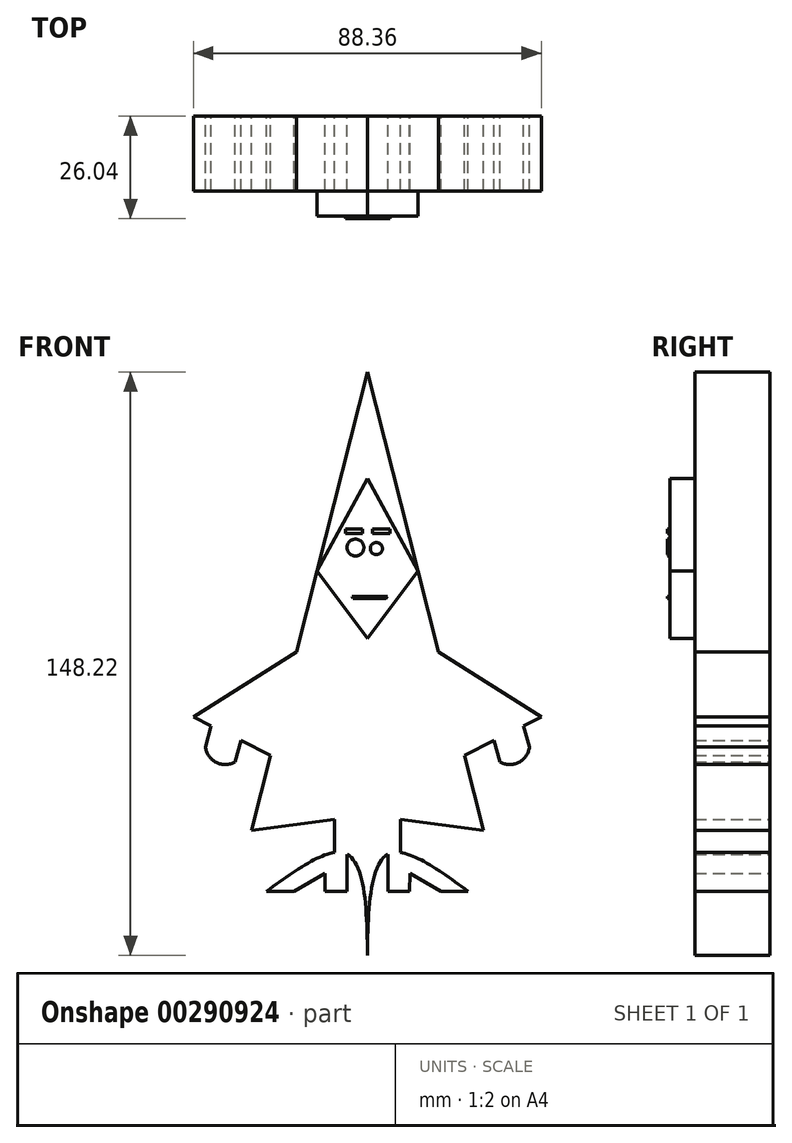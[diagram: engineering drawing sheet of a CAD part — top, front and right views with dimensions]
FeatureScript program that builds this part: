
annotation { "Feature Type Name" : "Feature", "Feature Type Description" : "" }
export const myFeature = defineFeature(function(context is Context, id is Id, definition is map)
    precondition{}
    {
        {
            var Q0;
            Q0=qCreatedBy(makeId("Front.planeOp"),FACE);
            var sketch = newSketch(context, id + "F0", { "sketchPlane" : qUnion([Q0])});
            skLineSegment(sketch, "E0", {"start": v(0, 75.5) * mm, "end": v(-12.78, 24.98) * mm});
            skLineSegment(sketch, "E1", {"start": v(-12.78, 24.98) * mm, "end": v(-17.99, 4.4) * mm});
            skLineSegment(sketch, "E2.MirrorCS", {"start": v(0, 75.5) * mm, "end": v(12.78, 24.98) * mm});
            skLineSegment(sketch, "E3.MirrorCS", {"start": v(12.78, 24.98) * mm, "end": v(17.99, 4.4) * mm});
            skLineSegment(sketch, "E4", {"start": v(-29.46, -40.92) * mm, "end": v(-8.36, -38.13) * mm});
            skLineSegment(sketch, "E5", {"start": v(-5.19, -37.7) * mm, "end": v(-5.19, -56.4) * mm});
            skLineSegment(sketch, "E6", {"start": v(-5.19, -56.4) * mm, "end": v(-10.75, -56.4) * mm});
            skLineSegment(sketch, "E7", {"start": v(-10.75, -56.4) * mm, "end": v(-10.75, -51.88) * mm});
            skLineSegment(sketch, "E8", {"start": v(-10.75, -51.88) * mm, "end": v(-18.7, -56.4) * mm});
            skLineSegment(sketch, "E9", {"start": v(-18.7, -56.4) * mm, "end": v(-25.6, -56.4) * mm});
            skFitSpline(sketch, "E10", {"points": [v(-25.6, -56.4) * mm, v(-5.19, -47.05) * mm, v(0, -78.15) * mm], "startDerivative": vector(52.64, 38.2) * mm, "endDerivative": vector(0.06, -78.44) * mm});
            skLineSegment(sketch, "E11", {"start": v(-8.36, -46.59) * mm, "end": v(-8.36, -38.13) * mm});
            skLineSegment(sketch, "E12", {"start": v(-17.99, 4.4) * mm, "end": v(-44.18, -12.07) * mm});
            skLineSegment(sketch, "E13", {"start": v(-44.18, -12.07) * mm, "end": v(-39.68, -14.35) * mm});
            skLineSegment(sketch, "E14", {"start": v(17.99, 4.4) * mm, "end": v(44.18, -12.07) * mm});
            skLineSegment(sketch, "E15", {"start": v(24.65, -21.93) * mm, "end": v(32.15, -18.15) * mm});
            skLineSegment(sketch, "E16.MirrorCS", {"start": v(5.19, -37.71) * mm, "end": v(5.17, -56.4) * mm});
            skLineSegment(sketch, "E17.MirrorCS", {"start": v(5.17, -56.4) * mm, "end": v(10.73, -56.4) * mm});
            skLineSegment(sketch, "E18.MirrorCS", {"start": v(8.35, -46.6) * mm, "end": v(8.36, -38.13) * mm});
            skFitSpline(sketch, "E19.MirrorCS", {"points": [v(25.6, -56.41) * mm, v(5.18, -47.05) * mm, v(-0.04, -78.15) * mm], "startDerivative": vector(-52.6, 38.25) * mm, "endDerivative": vector(-0.13, -78.44) * mm});
            skLineSegment(sketch, "E20.MirrorCS", {"start": v(10.73, -51.89) * mm, "end": v(18.7, -56.4) * mm});
            skLineSegment(sketch, "E21.MirrorCS", {"start": v(18.7, -56.4) * mm, "end": v(25.6, -56.41) * mm});
            skLineSegment(sketch, "E22.MirrorCS", {"start": v(10.73, -56.4) * mm, "end": v(10.73, -51.89) * mm});
            skLineSegment(sketch, "E23.trimOffspring", {"start": v(-24.65, -21.93) * mm, "end": v(-29.46, -40.92) * mm});
            skLineSegment(sketch, "E24.trimOffspring", {"start": v(24.65, -21.93) * mm, "end": v(29.46, -40.92) * mm});
            skLineSegment(sketch, "E25.trimOffspring", {"start": v(-5.19, -37.7) * mm, "end": v(0, -37.02) * mm});
            skLineSegment(sketch, "E26", {"start": v(0, -37.02) * mm, "end": v(5.19, -37.71) * mm});
            skLineSegment(sketch, "E27", {"start": v(8.36, -38.13) * mm, "end": v(29.46, -40.92) * mm});
            skLineSegment(sketch, "E28.trimOffspring", {"start": v(-32.15, -18.15) * mm, "end": v(-24.65, -21.93) * mm});
            skLineSegment(sketch, "E29.trimOffspring", {"start": v(39.68, -14.35) * mm, "end": v(44.18, -12.07) * mm});
            skLineSegment(sketch, "E30", {"start": v(-17.99, 4.4) * mm, "end": v(17.99, 4.4) * mm});
            skLineSegment(sketch, "E31", {"start": v(-39.68, -14.35) * mm, "end": v(-41.14, -19.7) * mm});
            skLineSegment(sketch, "E32", {"start": v(-32.15, -18.15) * mm, "end": v(-33.61, -23.5) * mm});
            skArc(sketch, "E33", {"start": v(-41.14, -19.7) * mm, "mid": v(-38.41, -23.67) * mm, "end": v(-33.61, -23.5) * mm});
            skLineSegment(sketch, "E34.MirrorCS", {"start": v(32.15, -18.15) * mm, "end": v(33.61, -23.5) * mm});
            skArc(sketch, "E35.MirrorCS", {"start": v(41.14, -19.7) * mm, "mid": v(38.41, -23.67) * mm, "end": v(33.61, -23.5) * mm});
            skLineSegment(sketch, "E36.MirrorCS", {"start": v(39.68, -14.35) * mm, "end": v(41.14, -19.7) * mm});
            skPoint(sketch, "E37.start.orphan", {"position": v(0, -5.3) * mm});
            skSolve(sketch);
        }
        {
            var Q0;
            Q0 = qSketchRegion(id + "F0", true);
            extrude(context, id + "F1", {"entities" : qUnion([Q0]), "depth" : 19.05 * mm});
        }
        {
            var Q0;
            Q0=makeQuery(id+"F1.opExtrude","CAP_FACE",FACE,{"disambiguationData":[OSD([sQuery(id+"F0.wireOp",EDGE,"E0"),sQuery(id+"F0.wireOp",EDGE,"E1"),sQuery(id+"F0.wireOp",EDGE,"E2.MirrorCS"),sQuery(id+"F0.wireOp",EDGE,"E3.MirrorCS"),sQuery(id+"F0.wireOp",EDGE,"E4"),sQuery(id+"F0.wireOp",EDGE,"E5"),sQuery(id+"F0.wireOp",EDGE,"E6"),sQuery(id+"F0.wireOp",EDGE,"E7"),sQuery(id+"F0.wireOp",EDGE,"E8"),sQuery(id+"F0.wireOp",EDGE,"E9"),sQuery(id+"F0.wireOp",EDGE,"E10"),sQuery(id+"F0.wireOp",EDGE,"E11"),sQuery(id+"F0.wireOp",EDGE,"E12"),sQuery(id+"F0.wireOp",EDGE,"E13"),sQuery(id+"F0.wireOp",EDGE,"E14"),sQuery(id+"F0.wireOp",EDGE,"E15"),sQuery(id+"F0.wireOp",EDGE,"E16.MirrorCS"),sQuery(id+"F0.wireOp",EDGE,"E17.MirrorCS"),sQuery(id+"F0.wireOp",EDGE,"E18.MirrorCS"),sQuery(id+"F0.wireOp",EDGE,"E19.MirrorCS"),sQuery(id+"F0.wireOp",EDGE,"E20.MirrorCS"),sQuery(id+"F0.wireOp",EDGE,"E21.MirrorCS"),sQuery(id+"F0.wireOp",EDGE,"E22.MirrorCS"),sQuery(id+"F0.wireOp",EDGE,"E23.trimOffspring"),sQuery(id+"F0.wireOp",EDGE,"E24.trimOffspring"),sQuery(id+"F0.wireOp",EDGE,"E25.trimOffspring"),sQuery(id+"F0.wireOp",EDGE,"E26"),sQuery(id+"F0.wireOp",EDGE,"E27")])],"isStart":false});
            var sketch = newSketch(context, id + "F2", { "sketchPlane" : qUnion([Q0])});
            skLineSegment(sketch, "E38", {"start": v(0, 48.43) * mm, "end": v(-12.78, 25) * mm});
            skLineSegment(sketch, "E39", {"start": v(-12.78, 25) * mm, "end": v(0, 7.83) * mm});
            skLineSegment(sketch, "E40", {"start": v(0, 7.83) * mm, "end": v(12.78, 25) * mm});
            skLineSegment(sketch, "E41", {"start": v(12.78, 25) * mm, "end": v(0, 48.43) * mm});
            skLineSegment(sketch, "E42", {"start": v(-17.99, 4.4) * mm, "end": v(-29.46, -40.92) * mm});
            skLineSegment(sketch, "E43", {"start": v(17.99, 4.4) * mm, "end": v(24.65, -21.93) * mm});
            skSolve(sketch);
        }
        {
            var Q0;
            Q0 = qSketchRegion(id + "F2", true);
            extrude(context, id + "F3", {"entities" : qUnion([Q0]), "operationType" : NewBodyOperationType.ADD, "depth" : 6.35 * mm});
        }
        {
            var Q0;
            Q0=makeQuery(id+"F3.opExtrude","CAP_FACE",FACE,{"disambiguationData":[OSD([sQuery(id+"F2.wireOp",EDGE,"E38"),sQuery(id+"F2.wireOp",EDGE,"E39"),sQuery(id+"F2.wireOp",EDGE,"E40"),sQuery(id+"F2.wireOp",EDGE,"E41")])],"isStart":false});
            var sketch = newSketch(context, id + "F4", { "sketchPlane" : qUnion([Q0])});
            skCircle(sketch, "E44", {"center": v(-3.05, 30.92) * mm, "radius": 2.14 * mm});
            skCircle(sketch, "E45", {"center": v(2.26, 30.65) * mm, "radius": 1.55 * mm});
            skLineSegment(sketch, "E46", {"start": v(-4, 18.48) * mm, "end": v(5.07, 18.48) * mm});
            skLineSegment(sketch, "E47", {"start": v(-5.62, 35.66) * mm, "end": v(-1.24, 35.66) * mm});
            skLineSegment(sketch, "E48", {"start": v(1.3, 35.66) * mm, "end": v(5.7, 35.66) * mm});
            skLineSegment(sketch, "E49", {"start": v(-5.62, 35.66) * mm, "end": v(-5.62, 34.46) * mm});
            skLineSegment(sketch, "E50", {"start": v(-1.24, 34.46) * mm, "end": v(-1.24, 35.66) * mm});
            skLineSegment(sketch, "E51", {"start": v(-1.24, 34.46) * mm, "end": v(-5.62, 34.46) * mm});
            skLineSegment(sketch, "E52", {"start": v(1.3, 35.66) * mm, "end": v(1.3, 34.46) * mm});
            skLineSegment(sketch, "E53", {"start": v(5.7, 34.46) * mm, "end": v(5.7, 35.66) * mm});
            skLineSegment(sketch, "E54", {"start": v(5.7, 34.46) * mm, "end": v(1.3, 34.46) * mm});
            skLineSegment(sketch, "E55", {"start": v(-4, 18.48) * mm, "end": v(-3.63, 18) * mm});
            skLineSegment(sketch, "E56", {"start": v(-3.63, 18) * mm, "end": v(4.7, 18) * mm});
            skLineSegment(sketch, "E57", {"start": v(4.7, 18) * mm, "end": v(5.07, 18.48) * mm});
            skSolve(sketch);
        }
        {
            var Q0;
            Q0 = qSketchRegion(id + "F4", true);
            extrude(context, id + "F5", {"entities" : qUnion([Q0]), "operationType" : NewBodyOperationType.ADD, "depth" : 0.64 * mm});
        }
    });
